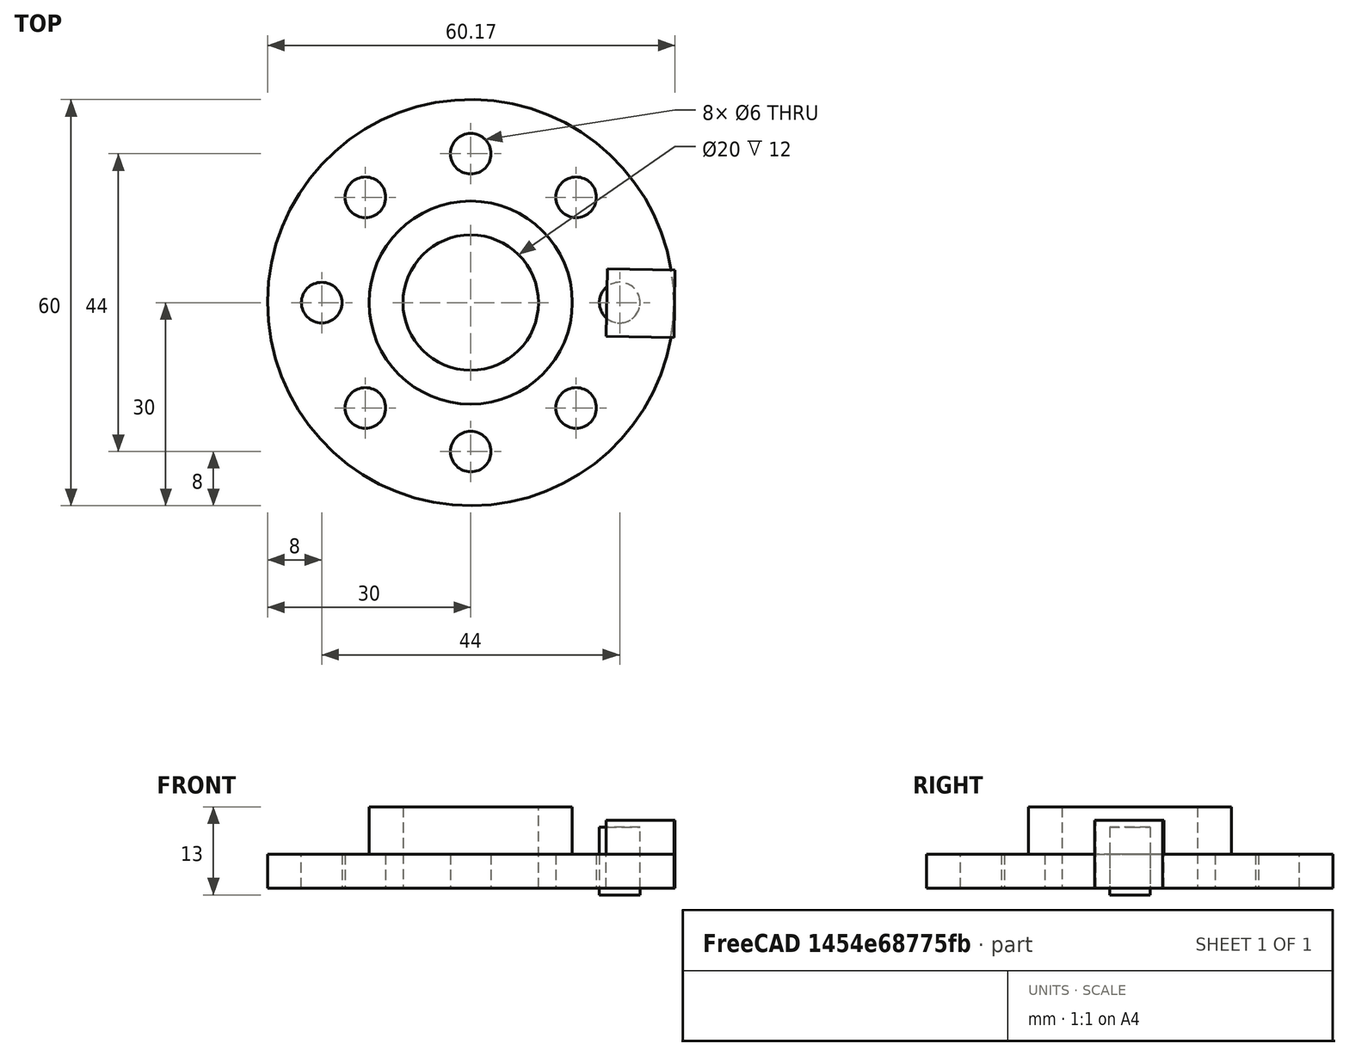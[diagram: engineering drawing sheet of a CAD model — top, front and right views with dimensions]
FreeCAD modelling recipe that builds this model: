
FCSTD DOCUMENT  (FreeCAD 0.21R33694 (Git))
Label: OJT1_T11P02_
License: All rights reserved
LicenseURL: http://en.wikipedia.org/wiki/All_rights_reserved
objects: Part::Cylinder×4, Part::Cut×3, Part::Fuse×2, Part::Box×1, Part::FeaturePython×1
note: 10 computed .brp shape members not serialized (recipe doc carries the construction recipe); baked Part::Feature solids carry a one-line shape summary decoded from their .brp

FEATURE [Part::Box] Box  label="Cube"
  AttacherType = Attacher::AttachEngine3D
  Height = 10
  Length = 10
  Placement = pos=(20,-5,0) rot=(0,0,1;-0.017453rad)
  Width = 10
FEATURE [Part::Cylinder] Cylinder
  Angle = 360
  AttacherType = Attacher::AttachEngine3D
  FirstAngle = 0
  Height = 5
  Radius = 30
  SecondAngle = 0
FEATURE [Part::Cylinder] Cylinder001
  Angle = 360
  AttacherType = Attacher::AttachEngine3D
  FirstAngle = 0
  Height = 12
  Radius = 15
  SecondAngle = 0
FEATURE [Part::Fuse] Fusion
  Base = -> Cylinder
  Refine = true
  Tool = -> Cylinder001
FEATURE [Part::Cylinder] Cylinder002
  Angle = 360
  AttacherType = Attacher::AttachEngine3D
  FirstAngle = 0
  Height = 30
  Radius = 10
  SecondAngle = 0
FEATURE [Part::Cut] Cut
  Base = -> Fusion
  Refine = true
  Tool = -> Cylinder002
FEATURE [Part::Cut] Cut001
  Base = -> Cylinder
  Refine = true
  Tool = -> Cylinder001
FEATURE [Part::Cylinder] Cylinder003
  Angle = 360
  AttacherType = Attacher::AttachEngine3D
  FirstAngle = 0
  Height = 10
  Placement = pos=(22,0,-1) rot=(0,0,1;0rad)
  Radius = 3
  SecondAngle = 0
FEATURE [Part::FeaturePython] Array001  # Draft array (typed FeaturePython)
  AlwaysSyncPlacement = false
  Angle = 360
  ArrayType = 1
  Axis = (0,0,1)
  Base = -> Cylinder003
  Center = (0,0,0)
  Count = 8
  ExpandArray = false
  Fuse = false
  IntervalAxis = (0,0,0)
  IntervalX = (100,0,0)
  IntervalY = (0,100,0)
  IntervalZ = (0,0,100)
  NumberCircles = 3
  NumberPolar = 8
  NumberX = 2
  NumberY = 2
  NumberZ = 1
  PlacementList = 8 placements: [(22,0,-1),(15.5563,15.5563,-1),(0,22,-1),(-15.5563,15.5563,-1),(-22,2.69422e-15,-1),(-15.5563,-15.5563,-1),(-4.88498e-15,-22,-1),(15.5563,-15.5563,-1)]
  RadialDistance = 50
  ScaleList = (8) [(1,1,1),(1,1,1),(1,1,1),(1,1,1),(1,1,1),(1,1,1),(1,1,1),(1,1,1)]
  Symmetry = 1
  TangentialDistance = 25
FEATURE [Part::Fuse] Fusion001
  Base = -> Cut
  Refine = true
  Tool = -> Cut001
FEATURE [Part::Cut] Cut002
  Base = -> Fusion001
  Refine = true
  Tool = -> Array001
